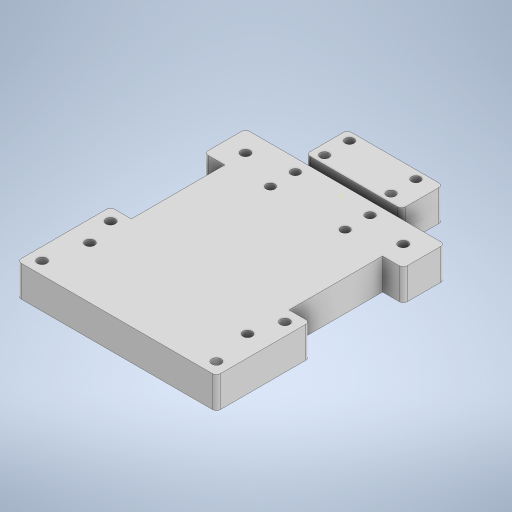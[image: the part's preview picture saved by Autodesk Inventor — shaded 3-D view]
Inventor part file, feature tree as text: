
AUTODESK INVENTOR PART (.ipt)
format: ipt  version: 2024 (Build 280153000, 153)  size: 320,000 bytes
history: native  units: mm
features: sketch x5, extrude x3, fillet x1, projected_geometry x1
ambient origin geometry x8: Origin, YZ Plane, XZ Plane, XY Plane, X Axis, Y Axis, Z Axis, Center Point
bodies: Solid1 (feature_tree)
feature tree (10):
  extrude  "Extrusion1"  Depth=110.0mm
  sketch  "Sketch2"  dims[d2=15.0mm d3=0.0mm d6=20.0mm]
  sketch  "Sketch3"  dims[d7=20.0mm d8=10.0mm d9=10.0mm]
  extrude  "Extrusion2"  Depth=20.0mm
  extrude  "Extrusion4"  Depth=10.0mm
  fillet  "Fillet1"  Radius=10.0mm
  sketch  "Sketch1"  dims[d0=96.0mm d1=110.0mm]
  sketch  "Sketch4"  dims[d10=45.0mm]
  projected_geometry  "Projected Loop1"
  sketch  "Sketch6"  dims[d11=45.0mm d12=15.0mm d13=0.0mm d19=20.0mm d20=20.0mm d21=10.0mm d22=10.0mm d23=18.0mm d24=18.0mm d25=20.0mm d26=20.0mm d27=4.2mm d28=4.2mm d29=6.0mm d30=25.0mm d31=25.0mm d32=4.1mm d33=20.0mm d34=4.0mm d35=4.0mm d36=4.0mm d37=4.0mm d38=12.0mm d39=12.0mm d40=15.0mm d41=0.0mm d42=2.0mm]
